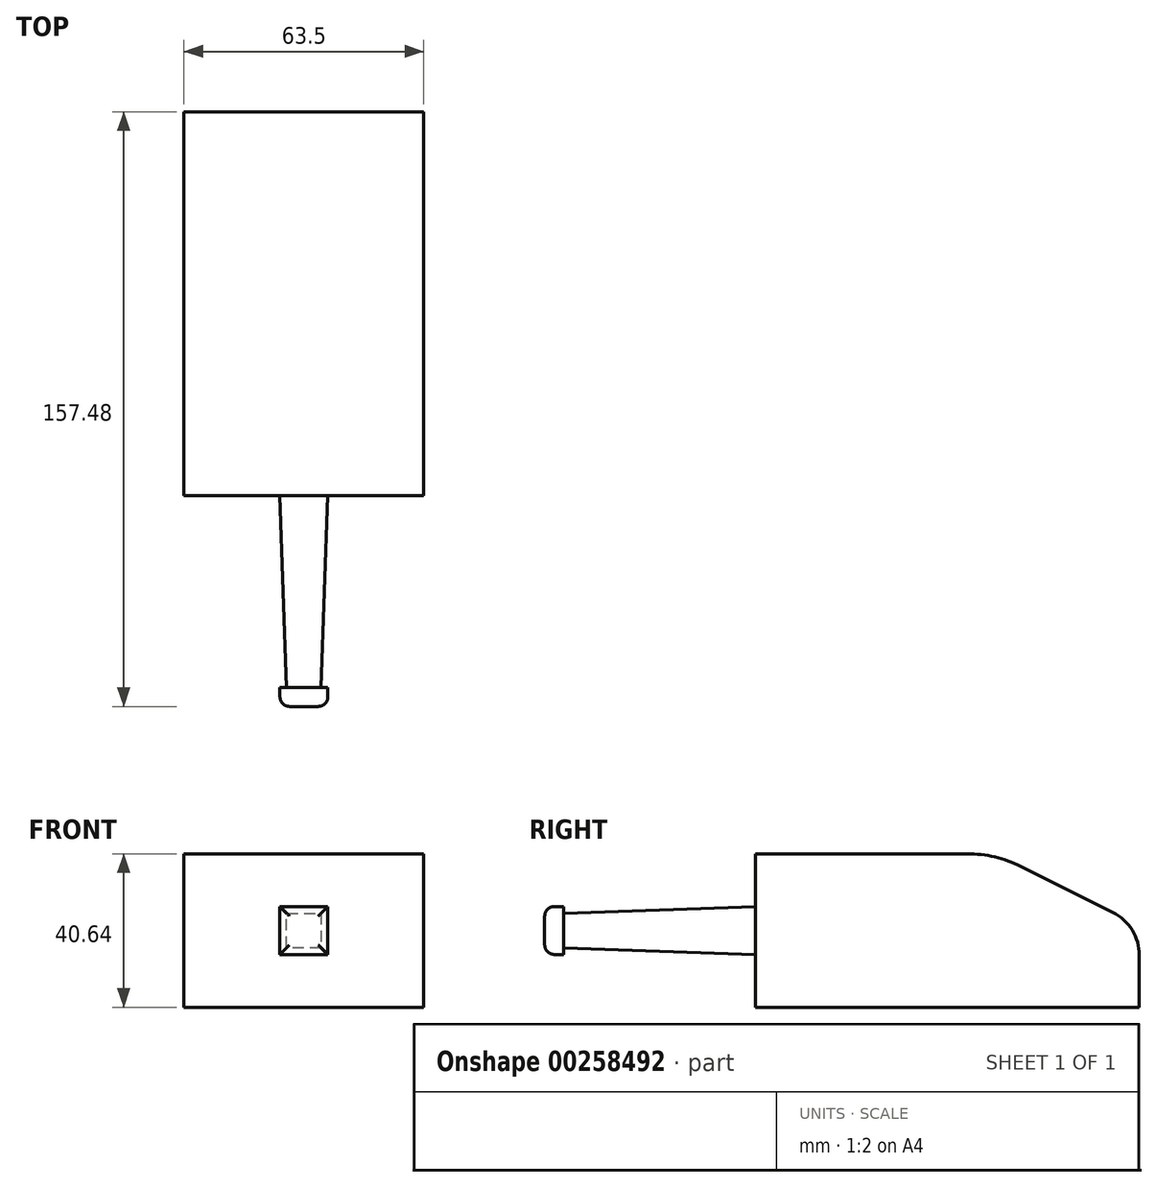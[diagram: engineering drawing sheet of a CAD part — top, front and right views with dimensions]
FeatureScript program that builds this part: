
annotation { "Feature Type Name" : "Feature", "Feature Type Description" : "" }
export const myFeature = defineFeature(function(context is Context, id is Id, definition is map)
    precondition{}
    {
        {
            var Q0;
            Q0=qCreatedBy(makeId("Right.planeOp"),FACE);
            var sketch = newSketch(context, id + "F0", { "sketchPlane" : qUnion([Q0])});
            skLineSegment(sketch, "E0", {"start": v(0, 0) * mm, "end": v(101.6, 0) * mm});
            skLineSegment(sketch, "E1", {"start": v(101.6, 0) * mm, "end": v(101.6, 13.74) * mm});
            skLineSegment(sketch, "E2", {"start": v(94.58, 25.1) * mm, "end": v(70.2, 37.29) * mm});
            skLineSegment(sketch, "E3", {"start": v(56, 40.64) * mm, "end": v(0, 40.64) * mm});
            skLineSegment(sketch, "E4", {"start": v(0, 40.64) * mm, "end": v(0, 0) * mm});
            skPoint(sketch, "E5.visualSharp", {"position": v(63.5, 40.64) * mm});
            skArc(sketch, "E5.filletArc", {"start": v(70.2, 37.29) * mm, "mid": v(63.3, 39.8) * mm, "end": v(56, 40.64) * mm});
            skPoint(sketch, "E6.visualSharp", {"position": v(101.6, 21.59) * mm});
            skArc(sketch, "E6.filletArc", {"start": v(101.6, 13.74) * mm, "mid": v(99.7, 20.42) * mm, "end": v(94.58, 25.1) * mm});
            skSolve(sketch);
        }
        {
            var Q0;
            Q0 = qSketchRegion(id + "F0", true);
            extrude(context, id + "F1", {"entities" : qUnion([Q0]), "depth" : 63.5 * mm});
        }
        {
            var Q0;
            Q0=makeQuery(id+"F1.opExtrude","SWEPT_FACE",FACE,{"disambiguationData":[OSD([sQuery(id+"F0.wireOp",EDGE,"E4")])]});
            var sketch = newSketch(context, id + "F2", { "sketchPlane" : qUnion([Q0])});
            skLineSegment(sketch, "E7", {"start": v(31.75, 40.64) * mm, "end": v(31.75, 0) * mm, "construction": true});
            skLineSegment(sketch, "E8", {"start": v(0, 20.32) * mm, "end": v(63.5, 20.32) * mm, "construction": true});
            skLineSegment(sketch, "E9.bottom", {"start": v(25.4, 26.67) * mm, "end": v(38.1, 26.67) * mm});
            skLineSegment(sketch, "E9.top", {"start": v(25.4, 13.97) * mm, "end": v(38.1, 13.97) * mm});
            skLineSegment(sketch, "E9.left", {"start": v(25.4, 26.67) * mm, "end": v(25.4, 13.97) * mm});
            skLineSegment(sketch, "E9.right", {"start": v(38.1, 26.67) * mm, "end": v(38.1, 13.97) * mm});
            skPoint(sketch, "E9.middle", {"position": v(31.75, 20.32) * mm});
            skSolve(sketch);
        }
        {
            var Q0;
            Q0 = qSketchRegion(id + "F2", true);
            extrude(context, id + "F3", {"entities" : qUnion([Q0]), "operationType" : NewBodyOperationType.ADD, "depth" : 50.8 * mm, "hasDraft" : true, "draftAngle" : 2 * degree, "draftPullDirection" : true});
        }
        {
            var Q0;
            Q0=makeQuery(id+"F3.opExtrude","CAP_FACE",FACE,{"disambiguationData":[OSD([sQuery(id+"F2.wireOp",EDGE,"E9.bottom"),sQuery(id+"F2.wireOp",EDGE,"E9.top"),sQuery(id+"F2.wireOp",EDGE,"E9.left"),sQuery(id+"F2.wireOp",EDGE,"E9.right")])],"isStart":false});
            var sketch = newSketch(context, id + "F4", { "sketchPlane" : qUnion([Q0])});
            skLineSegment(sketch, "E10", {"start": v(27.17, 20.32) * mm, "end": v(36.33, 20.32) * mm, "construction": true});
            skLineSegment(sketch, "E11", {"start": v(31.75, 15.74) * mm, "end": v(31.75, 24.9) * mm, "construction": true});
            skLineSegment(sketch, "E12.bottom", {"start": v(25.4, 26.67) * mm, "end": v(38.1, 26.67) * mm});
            skLineSegment(sketch, "E12.top", {"start": v(25.4, 13.97) * mm, "end": v(38.1, 13.97) * mm});
            skLineSegment(sketch, "E12.left", {"start": v(25.4, 26.67) * mm, "end": v(25.4, 13.97) * mm});
            skLineSegment(sketch, "E12.right", {"start": v(38.1, 26.67) * mm, "end": v(38.1, 13.97) * mm});
            skPoint(sketch, "E12.middle", {"position": v(31.75, 20.32) * mm});
            skSolve(sketch);
        }
        {
            var Q0;
            Q0 = qSketchRegion(id + "F4", true);
            extrude(context, id + "F5", {"entities" : qUnion([Q0]), "operationType" : NewBodyOperationType.ADD, "depth" : 5.08 * mm});
        }
        {
            var Q0;
            Q0=makeQuery(id+"F5.opExtrude","CAP_EDGE",EDGE,{"disambiguationData":[OSD([sQuery(id+"F4.wireOp",EDGE,"E12.bottom")])],"isStart":false});
            var Q1;
            Q1=makeQuery(id+"F5.opExtrude","CAP_EDGE",EDGE,{"disambiguationData":[OSD([sQuery(id+"F4.wireOp",EDGE,"E12.right")])],"isStart":false});
            var Q2;
            Q2=makeQuery(id+"F5.opExtrude","CAP_EDGE",EDGE,{"disambiguationData":[OSD([sQuery(id+"F4.wireOp",EDGE,"E12.top")])],"isStart":false});
            var Q3;
            Q3=makeQuery(id+"F5.opExtrude","CAP_EDGE",EDGE,{"disambiguationData":[OSD([sQuery(id+"F4.wireOp",EDGE,"E12.left")])],"isStart":false});
            var Q4;
            Q4=makeQuery(id+"F3.opExtrude","CAP_EDGE",EDGE,{"disambiguationData":[OSD([sQuery(id+"F2.wireOp",EDGE,"E9.right")])],"isStart":false});
            var Q5;
            Q5=makeQuery(id+"F3.opExtrude","CAP_EDGE",EDGE,{"disambiguationData":[OSD([sQuery(id+"F2.wireOp",EDGE,"E9.bottom")])],"isStart":false});
            var Q6;
            Q6=makeQuery(id+"F3.opExtrude","CAP_EDGE",EDGE,{"disambiguationData":[OSD([sQuery(id+"F2.wireOp",EDGE,"E9.left")])],"isStart":false});
            var Q7;
            Q7=makeQuery(id+"F3.opExtrude","CAP_EDGE",EDGE,{"disambiguationData":[OSD([sQuery(id+"F2.wireOp",EDGE,"E9.top")])],"isStart":false});
            fillet(context, id + "F6", {"entities" : qUnion([Q0, Q1, Q2, Q3, Q4, Q5, Q6, Q7]), "radius" : 2.54 * mm, "tangentPropagation" : true, "allowEdgeOverflow" : false});
        }
    });
